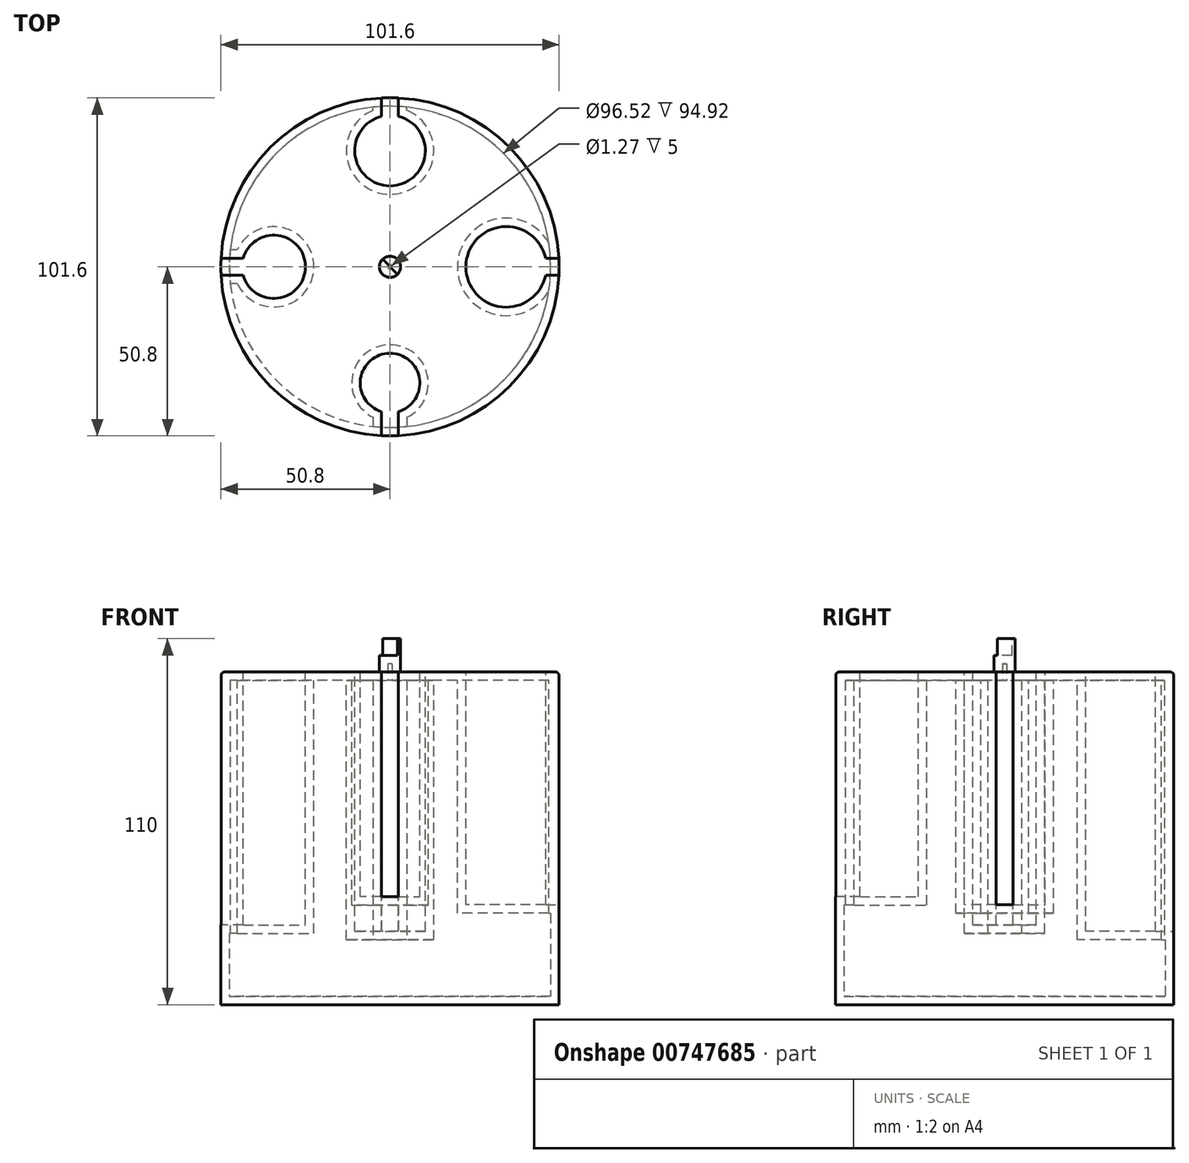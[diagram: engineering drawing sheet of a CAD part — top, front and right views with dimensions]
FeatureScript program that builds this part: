
annotation { "Feature Type Name" : "Feature", "Feature Type Description" : "" }
export const myFeature = defineFeature(function(context is Context, id is Id, definition is map)
    precondition{}
    {
        {
            var Q0;
            Q0=qCreatedBy(makeId("Top.planeOp"),FACE);
            var sketch = newSketch(context, id + "F0", { "sketchPlane" : qUnion([Q0])});
            skCircle(sketch, "E0", {"center": v(0, 0) * mm, "radius": 50.8 * mm});
            skSolve(sketch);
        }
        {
            var Q0;
            Q0 = qSketchRegion(id + "F0", true);
            extrude(context, id + "F1", {"entities" : qUnion([Q0]), "depth" : 100 * mm, "offsetDistance" : 25.4 * mm});
        }
        {
            var Q0;
            Q0=makeQuery(id+"F1.opExtrude","CAP_FACE",FACE,{"disambiguationData":[OSD([sQuery(id+"F0.wireOp",EDGE,"E0")])],"isStart":false});
            var sketch = newSketch(context, id + "F2", { "sketchPlane" : qUnion([Q0])});
            skArc(sketch, "E1", {"start": v(32.82, 11.95) * mm, "mid": v(-34.93, 0) * mm, "end": v(32.82, -11.95) * mm});
            skArc(sketch, "E2", {"start": v(46.79, 2.54) * mm, "mid": v(22.8, 0) * mm, "end": v(46.79, -2.54) * mm});
            skCircle(sketch, "E3", {"center": v(0, 0) * mm, "radius": 50.8 * mm});
            skLineSegment(sketch, "E4.0", {"start": v(46.79, -2.54) * mm, "end": v(50.74, -2.54) * mm});
            skLineSegment(sketch, "E5.0", {"start": v(46.79, 2.54) * mm, "end": v(50.74, 2.54) * mm});
            skSolve(sketch);
        }
        {
            var Q0;
            {var subQ0=sQuery(id+"F2.wireOp",EDGE,"E4.0");Q0=makeQuery(id+"F2.imprint","IMPRINT",FACE,{"disambiguationData":[TD([[makeQuery(id+"F2.imprint","IMPRINT",EDGE,{"derivedFrom":subQ0}),1.0]])]});}
            extrude(context, id + "F3", {"entities" : qUnion([Q0]), "operationType" : NewBodyOperationType.REMOVE, "oppositeDirection" : true, "depth" : 70 * mm, "offsetDistance" : 25.4 * mm});
        }
        {
            var Q0;
            Q0=makeQuery(id+"F1.opExtrude","CAP_FACE",FACE,{"disambiguationData":[OSD([sQuery(id+"F0.wireOp",EDGE,"E0")])],"isStart":false});
            var sketch = newSketch(context, id + "F4", { "sketchPlane" : qUnion([Q0])});
            skArc(sketch, "E6", {"start": v(-10.48, 33.31) * mm, "mid": v(0, -34.92) * mm, "end": v(10.48, 33.31) * mm});
            skArc(sketch, "E7", {"start": v(-2.54, 45.22) * mm, "mid": v(0, 24.32) * mm, "end": v(2.54, 45.22) * mm});
            skArc(sketch, "E8", {"start": v(-2.54, 50.7) * mm, "mid": v(0, -50.76) * mm, "end": v(2.54, 50.7) * mm});
            skLineSegment(sketch, "E9.0", {"start": v(2.54, 45.22) * mm, "end": v(2.54, 50.7) * mm});
            skLineSegment(sketch, "E10.0", {"start": v(-2.54, 45.22) * mm, "end": v(-2.54, 50.7) * mm});
            skLineSegment(sketch, "E11.top", {"start": v(-2.54, 55.74) * mm, "end": v(2.54, 55.74) * mm});
            skLineSegment(sketch, "E11.left", {"start": v(-2.54, 50.7) * mm, "end": v(-2.54, 55.74) * mm});
            skLineSegment(sketch, "E11.right", {"start": v(2.54, 50.7) * mm, "end": v(2.54, 55.74) * mm});
            skSolve(sketch);
        }
        {
            var Q0;
            {var subQ3=sQuery(id+"F4.wireOp",EDGE,"E9.0");Q0=makeQuery(id+"F4.imprint","IMPRINT",FACE,{"disambiguationData":[TD([[makeQuery(id+"F4.imprint","IMPRINT",EDGE,{"derivedFrom":subQ3}),1.0]])]});}
            var Q1;
            {var subQ0=sQuery(id+"F4.wireOp",EDGE,"E11.top");Q1=makeQuery(id+"F4.imprint","IMPRINT",FACE,{"disambiguationData":[TD([[makeQuery(id+"F4.imprint","IMPRINT",EDGE,{"derivedFrom":subQ0}),-1.0]])]});}
            extrude(context, id + "F5", {"entities" : qUnion([Q0, Q1]), "operationType" : NewBodyOperationType.REMOVE, "oppositeDirection" : true, "depth" : 78 * mm, "offsetDistance" : 25.4 * mm});
        }
        {
            var Q0;
            Q0=makeQuery(id+"F1.opExtrude","CAP_FACE",FACE,{"disambiguationData":[OSD([sQuery(id+"F0.wireOp",EDGE,"E0")])],"isStart":false});
            var sketch = newSketch(context, id + "F6", { "sketchPlane" : qUnion([Q0])});
            skArc(sketch, "E12", {"start": v(-33.63, -9.44) * mm, "mid": v(34.93, 0) * mm, "end": v(-33.63, 9.44) * mm});
            skArc(sketch, "E13", {"start": v(-44.1, -2.54) * mm, "mid": v(-25.4, 0) * mm, "end": v(-44.1, 2.54) * mm});
            skCircle(sketch, "E14", {"center": v(0, 0) * mm, "radius": 50.8 * mm});
            skLineSegment(sketch, "E15.0", {"start": v(-44.1, 2.54) * mm, "end": v(-50.74, 2.54) * mm});
            skLineSegment(sketch, "E16.0", {"start": v(-44.1, -2.54) * mm, "end": v(-50.74, -2.54) * mm});
            skSolve(sketch);
        }
        {
            var Q0;
            {var subQ3=sQuery(id+"F6.wireOp",EDGE,"E15.0");Q0=makeQuery(id+"F6.imprint","IMPRINT",FACE,{"disambiguationData":[TD([[makeQuery(id+"F6.imprint","IMPRINT",EDGE,{"derivedFrom":subQ3}),1.0]])]});}
            extrude(context, id + "F7", {"entities" : qUnion([Q0]), "operationType" : NewBodyOperationType.REMOVE, "oppositeDirection" : true, "depth" : 76 * mm, "offsetDistance" : 25.4 * mm});
        }
        {
            var Q0;
            Q0=makeQuery(id+"F1.opExtrude","CAP_FACE",FACE,{"disambiguationData":[OSD([sQuery(id+"F0.wireOp",EDGE,"E0")])],"isStart":false});
            var sketch = newSketch(context, id + "F8", { "sketchPlane" : qUnion([Q0])});
            skArc(sketch, "E17", {"start": v(8.88, -33.78) * mm, "mid": v(0, 34.93) * mm, "end": v(-8.88, -33.78) * mm});
            skCircle(sketch, "E18", {"center": v(0, 0) * mm, "radius": 50.8 * mm});
            skArc(sketch, "E19", {"start": v(2.54, -43.51) * mm, "mid": v(0, -25.97) * mm, "end": v(-2.54, -43.51) * mm});
            skLineSegment(sketch, "E20.0", {"start": v(-2.54, -43.51) * mm, "end": v(-2.54, -50.74) * mm});
            skLineSegment(sketch, "E21.0", {"start": v(2.54, -43.51) * mm, "end": v(2.54, -50.74) * mm});
            skSolve(sketch);
        }
        {
            var Q0;
            {var subQ5=sQuery(id+"F8.wireOp",EDGE,"E20.0");Q0=makeQuery(id+"F8.imprint","IMPRINT",FACE,{"disambiguationData":[TD([[makeQuery(id+"F8.imprint","IMPRINT",EDGE,{"derivedFrom":subQ5}),1.0]])]});}
            extrude(context, id + "F9", {"entities" : qUnion([Q0]), "operationType" : NewBodyOperationType.REMOVE, "oppositeDirection" : true, "depth" : 67.5 * mm, "offsetDistance" : 25.4 * mm});
        }
        {
            var Q0;
            Q0=makeQuery(id+"F1.opExtrude","CAP_FACE",FACE,{"disambiguationData":[OSD([sQuery(id+"F0.wireOp",EDGE,"E0")])],"isStart":false});
            var sketch = newSketch(context, id + "F10", { "sketchPlane" : qUnion([Q0])});
            skCircle(sketch, "E22", {"center": v(0, 0) * mm, "radius": 3.18 * mm});
            skSolve(sketch);
        }
        {
            var Q0;
            Q0 = qSketchRegion(id + "F10", true);
            extrude(context, id + "F11", {"entities" : qUnion([Q0]), "operationType" : NewBodyOperationType.ADD, "depth" : 10 * mm, "offsetDistance" : 25.4 * mm});
        }
        {
            var Q0;
            Q0=makeQuery(id+"F11.opExtrude","CAP_FACE",FACE,{"disambiguationData":[OSD([sQuery(id+"F10.wireOp",EDGE,"E22")])],"isStart":false});
            var sketch = newSketch(context, id + "F12", { "sketchPlane" : qUnion([Q0])});
            skCircle(sketch, "E23", {"center": v(0, 0) * mm, "radius": 3.18 * mm});
            skLineSegment(sketch, "E24", {"start": v(-2.25, 2.25) * mm, "end": v(0, 0) * mm});
            skLineSegment(sketch, "E25", {"start": v(2.25, -2.25) * mm, "end": v(0, 0) * mm});
            skPoint(sketch, "E26.start.orphan", {"position": v(-3.18, 0) * mm});
            skSolve(sketch);
        }
        {
            var Q0;
            {var subQ0=sQuery(id+"F12.wireOp",EDGE,"E24");Q0=makeQuery(id+"F12.imprint","IMPRINT",FACE,{"disambiguationData":[TD([[makeQuery(id+"F12.imprint","IMPRINT",EDGE,{"derivedFrom":subQ0}),-1.0]])]});}
            extrude(context, id + "F13", {"entities" : qUnion([Q0]), "operationType" : NewBodyOperationType.REMOVE, "oppositeDirection" : true, "depth" : 5 * mm, "offsetDistance" : 25.4 * mm});
        }
        {
            var Q0;
            Q0=makeQuery(id+"F9.boolean.opBoolean","COPY",EDGE,{"derivedFrom":makeQuery(id+"F9.opExtrude","CAP_EDGE",EDGE,{"disambiguationData":[OSD([sQuery(id+"F8.wireOp",EDGE,"E19")])],"isStart":true})});
            var Q1;
            Q1=makeQuery(id+"F7.boolean.opBoolean","COPY",EDGE,{"derivedFrom":makeQuery(id+"F7.opExtrude","CAP_EDGE",EDGE,{"disambiguationData":[OSD([sQuery(id+"F6.wireOp",EDGE,"E13")])],"isStart":true})});
            var Q2;
            Q2=makeQuery(id+"F5.boolean.opBoolean","COPY",EDGE,{"derivedFrom":makeQuery(id+"F5.opExtrude","CAP_EDGE",EDGE,{"disambiguationData":[OSD([sQuery(id+"F4.wireOp",EDGE,"E7")])],"isStart":true})});
            var Q3;
            {var subQ0=sQuery(id+"F0.wireOp",EDGE,"E0");var subQ2=makeQuery(id+"F7.opExtrude","SWEPT_FACE",FACE,{"disambiguationData":[OSD([sQuery(id+"F6.wireOp",EDGE,"E16.0")])]});var subQ4=makeQuery(id+"F3.boolean.opBoolean","COPY",FACE,{"derivedFrom":makeQuery(id+"F3.opExtrude","SWEPT_FACE",FACE,{"disambiguationData":[OSD([sQuery(id+"F2.wireOp",EDGE,"E4.0")])]})});Q3=makeQuery(id+"F9.boolean.opBoolean","SPLIT",EDGE,{"disambiguationData":[TD([makeQuery(id+"F7.boolean.opBoolean","COPY",FACE,{"derivedFrom":subQ2})])],"derivedFrom":makeQuery(id+"F7.boolean.opBoolean","SPLIT",EDGE,{"disambiguationData":[TD([subQ4])],"derivedFrom":makeQuery(id+"F5.boolean.opBoolean","SPLIT",EDGE,{"disambiguationData":[TD([subQ4])],"derivedFrom":makeQuery(id+"F1.opExtrude","CAP_EDGE",EDGE,{"disambiguationData":[OSD([subQ0])],"isStart":false})})})});}
            var Q4;
            {var subQ0=sQuery(id+"F0.wireOp",EDGE,"E0");Q4=makeQuery(id+"F7.boolean.opBoolean","SPLIT",EDGE,{"disambiguationData":[TD([makeQuery(id+"F7.opExtrude","SWEPT_FACE",FACE,{"disambiguationData":[OSD([sQuery(id+"F6.wireOp",EDGE,"E15.0")])]})])],"derivedFrom":makeQuery(id+"F5.boolean.opBoolean","SPLIT",EDGE,{"disambiguationData":[TD([makeQuery(id+"F3.boolean.opBoolean","COPY",FACE,{"derivedFrom":makeQuery(id+"F3.opExtrude","SWEPT_FACE",FACE,{"disambiguationData":[OSD([sQuery(id+"F2.wireOp",EDGE,"E4.0")])]})})])],"derivedFrom":makeQuery(id+"F1.opExtrude","CAP_EDGE",EDGE,{"disambiguationData":[OSD([subQ0])],"isStart":false})})});}
            var Q5;
            {var subQ0=sQuery(id+"F0.wireOp",EDGE,"E0");Q5=makeQuery(id+"F5.boolean.opBoolean","SPLIT",EDGE,{"disambiguationData":[TD([makeQuery(id+"F3.boolean.opBoolean","COPY",FACE,{"derivedFrom":makeQuery(id+"F3.opExtrude","SWEPT_FACE",FACE,{"disambiguationData":[OSD([sQuery(id+"F2.wireOp",EDGE,"E5.0")])]})})])],"derivedFrom":makeQuery(id+"F1.opExtrude","CAP_EDGE",EDGE,{"disambiguationData":[OSD([subQ0])],"isStart":false})});}
            var Q6;
            {var subQ0=sQuery(id+"F0.wireOp",EDGE,"E0");var subQ3=makeQuery(id+"F3.boolean.opBoolean","COPY",FACE,{"derivedFrom":makeQuery(id+"F3.opExtrude","SWEPT_FACE",FACE,{"disambiguationData":[OSD([sQuery(id+"F2.wireOp",EDGE,"E4.0")])]})});Q6=makeQuery(id+"F9.boolean.opBoolean","SPLIT",EDGE,{"disambiguationData":[TD([subQ3])],"derivedFrom":makeQuery(id+"F7.boolean.opBoolean","SPLIT",EDGE,{"disambiguationData":[TD([subQ3])],"derivedFrom":makeQuery(id+"F5.boolean.opBoolean","SPLIT",EDGE,{"disambiguationData":[TD([subQ3])],"derivedFrom":makeQuery(id+"F1.opExtrude","CAP_EDGE",EDGE,{"disambiguationData":[OSD([subQ0])],"isStart":false})})})});}
            var Q7;
            Q7=makeQuery(id+"F9.boolean.opBoolean","COPY",EDGE,{"derivedFrom":makeQuery(id+"F9.opExtrude","CAP_EDGE",EDGE,{"disambiguationData":[OSD([sQuery(id+"F8.wireOp",EDGE,"E20.0")])],"isStart":true})});
            var Q8;
            Q8=makeQuery(id+"F9.boolean.opBoolean","COPY",EDGE,{"derivedFrom":makeQuery(id+"F9.opExtrude","CAP_EDGE",EDGE,{"disambiguationData":[OSD([sQuery(id+"F8.wireOp",EDGE,"E21.0")])],"isStart":true})});
            var Q9;
            Q9=makeQuery(id+"F3.boolean.opBoolean","COPY",EDGE,{"derivedFrom":makeQuery(id+"F3.opExtrude","CAP_EDGE",EDGE,{"disambiguationData":[OSD([sQuery(id+"F2.wireOp",EDGE,"E4.0")])],"isStart":true})});
            var Q10;
            Q10=makeQuery(id+"F3.boolean.opBoolean","COPY",EDGE,{"derivedFrom":makeQuery(id+"F3.opExtrude","CAP_EDGE",EDGE,{"disambiguationData":[OSD([sQuery(id+"F2.wireOp",EDGE,"E2")])],"isStart":true})});
            var Q11;
            Q11=makeQuery(id+"F3.boolean.opBoolean","COPY",EDGE,{"derivedFrom":makeQuery(id+"F3.opExtrude","CAP_EDGE",EDGE,{"disambiguationData":[OSD([sQuery(id+"F2.wireOp",EDGE,"E5.0")])],"isStart":true})});
            var Q12;
            Q12=makeQuery(id+"F5.boolean.opBoolean","COPY",EDGE,{"derivedFrom":makeQuery(id+"F5.opExtrude","CAP_EDGE",EDGE,{"disambiguationData":[OSD([sQuery(id+"F4.wireOp",EDGE,"E9.0"),sQuery(id+"F4.wireOp",EDGE,"E11.right")])],"isStart":true})});
            var Q13;
            Q13=makeQuery(id+"F5.boolean.opBoolean","COPY",EDGE,{"derivedFrom":makeQuery(id+"F5.opExtrude","CAP_EDGE",EDGE,{"disambiguationData":[OSD([sQuery(id+"F4.wireOp",EDGE,"E10.0"),sQuery(id+"F4.wireOp",EDGE,"E11.left")])],"isStart":true})});
            var Q14;
            Q14=makeQuery(id+"F7.boolean.opBoolean","COPY",EDGE,{"derivedFrom":makeQuery(id+"F7.opExtrude","CAP_EDGE",EDGE,{"disambiguationData":[OSD([sQuery(id+"F6.wireOp",EDGE,"E16.0")])],"isStart":true})});
            var Q15;
            Q15=makeQuery(id+"F7.boolean.opBoolean","COPY",EDGE,{"derivedFrom":makeQuery(id+"F7.opExtrude","CAP_EDGE",EDGE,{"disambiguationData":[OSD([sQuery(id+"F6.wireOp",EDGE,"E15.0")])],"isStart":true})});
            fillet(context, id + "F14", {"entities" : qUnion([Q0, Q1, Q2, Q3, Q4, Q5, Q6, Q7, Q8, Q9, Q10, Q11, Q12, Q13, Q14, Q15]), "radius" : 1 * mm, "tangentPropagation" : true, "allowEdgeOverflow" : false});
        }
        {
            var Q0;
            Q0=makeQuery(id+"F1.opExtrude","CAP_FACE",FACE,{"disambiguationData":[OSD([sQuery(id+"F0.wireOp",EDGE,"E0")])],"isStart":true});
            var Q1;
            Q1=makeQuery(id+"F1.opExtrude","SWEPT_BODY",BODY,{"disambiguationData":[OSD([sQuery(id+"F0.wireOp",EDGE,"E0")])]});
            shell(context, id + "F15", {"isHollow" : true, "entities" : qUnion([Q0]), "parts" : qUnion([Q1]), "thickness" : 2.54 * mm});
        }
    });
